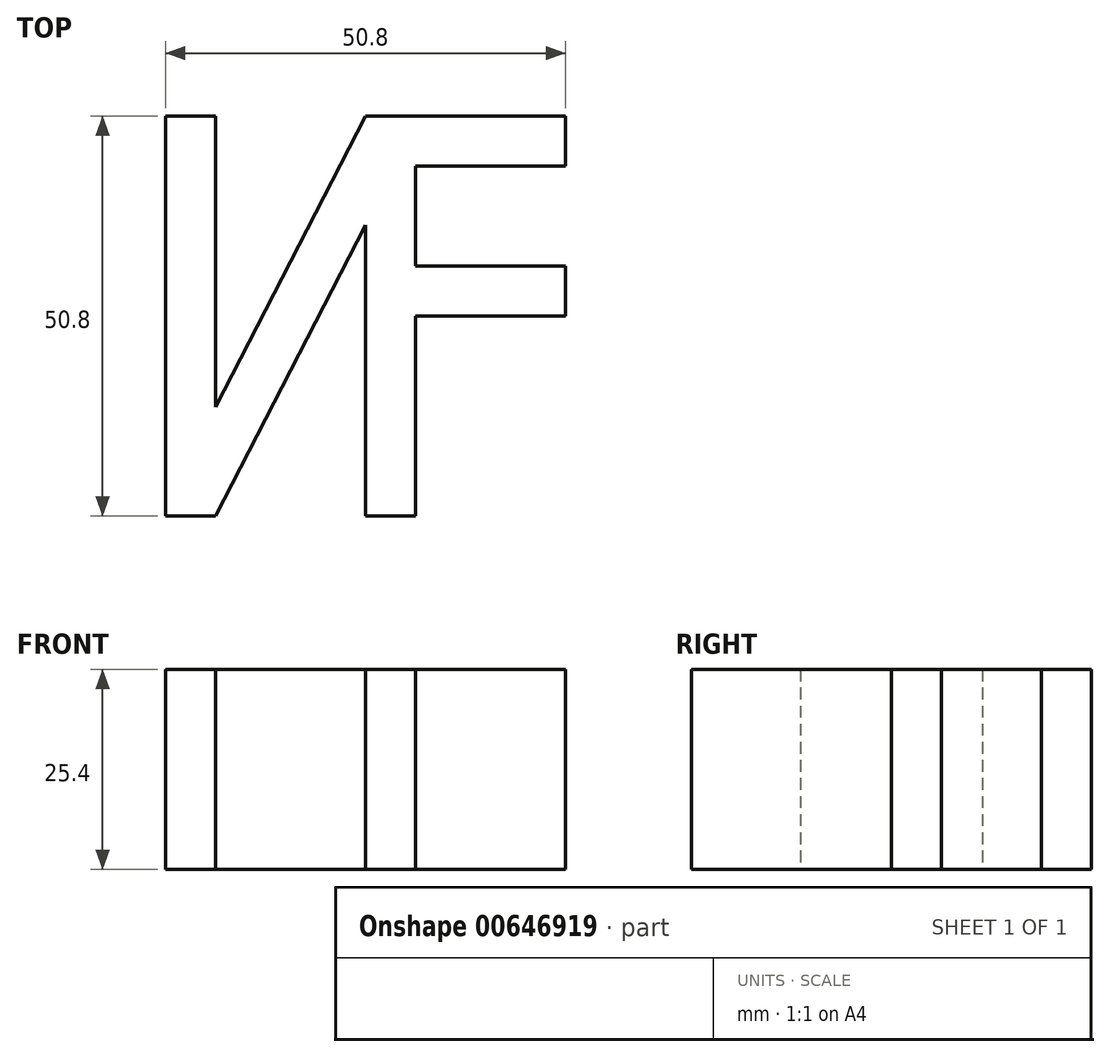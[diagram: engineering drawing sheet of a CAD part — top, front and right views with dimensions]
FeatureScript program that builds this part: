
annotation { "Feature Type Name" : "Feature", "Feature Type Description" : "" }
export const myFeature = defineFeature(function(context is Context, id is Id, definition is map)
    precondition{}
    {
        {
            var Q0;
            Q0=qCreatedBy(makeId("Top.planeOp"),FACE);
            var sketch = newSketch(context, id + "F0", { "sketchPlane" : qUnion([Q0])});
            skLineSegment(sketch, "E0", {"start": v(0, 0) * mm, "end": v(0, 50.8) * mm});
            skLineSegment(sketch, "E1", {"start": v(0, 50.8) * mm, "end": v(6.35, 50.8) * mm});
            skLineSegment(sketch, "E2", {"start": v(6.35, 50.8) * mm, "end": v(6.35, 0) * mm});
            skLineSegment(sketch, "E3", {"start": v(6.35, 0) * mm, "end": v(0, 0) * mm});
            skLineSegment(sketch, "E4", {"start": v(31.75, 50.8) * mm, "end": v(25.4, 50.8) * mm});
            skLineSegment(sketch, "E5", {"start": v(31.75, 50.8) * mm, "end": v(31.75, 0) * mm});
            skLineSegment(sketch, "E6", {"start": v(31.75, 0) * mm, "end": v(25.4, 0) * mm});
            skLineSegment(sketch, "E7", {"start": v(25.4, 0) * mm, "end": v(25.4, 50.8) * mm});
            skLineSegment(sketch, "E8", {"start": v(31.75, 50.8) * mm, "end": v(50.8, 50.8) * mm});
            skLineSegment(sketch, "E9", {"start": v(50.8, 50.8) * mm, "end": v(50.8, 44.45) * mm});
            skLineSegment(sketch, "E10", {"start": v(50.8, 44.45) * mm, "end": v(31.75, 44.45) * mm});
            skLineSegment(sketch, "E11", {"start": v(31.75, 31.75) * mm, "end": v(50.8, 31.75) * mm});
            skLineSegment(sketch, "E12", {"start": v(50.8, 31.75) * mm, "end": v(50.8, 25.4) * mm});
            skLineSegment(sketch, "E13", {"start": v(50.8, 25.4) * mm, "end": v(31.75, 25.4) * mm});
            skLineSegment(sketch, "E14", {"start": v(25.4, 50.8) * mm, "end": v(6.35, 13.86) * mm});
            skLineSegment(sketch, "E15", {"start": v(6.35, 0) * mm, "end": v(25.4, 36.94) * mm});
            skSolve(sketch);
        }
        {
            var Q0;
            Q0 = qSketchRegion(id + "F0", true);
            extrude(context, id + "F1", {"entities" : qUnion([Q0]), "depth" : 25.4 * mm, "offsetDistance" : 25.4 * mm});
        }
    });
